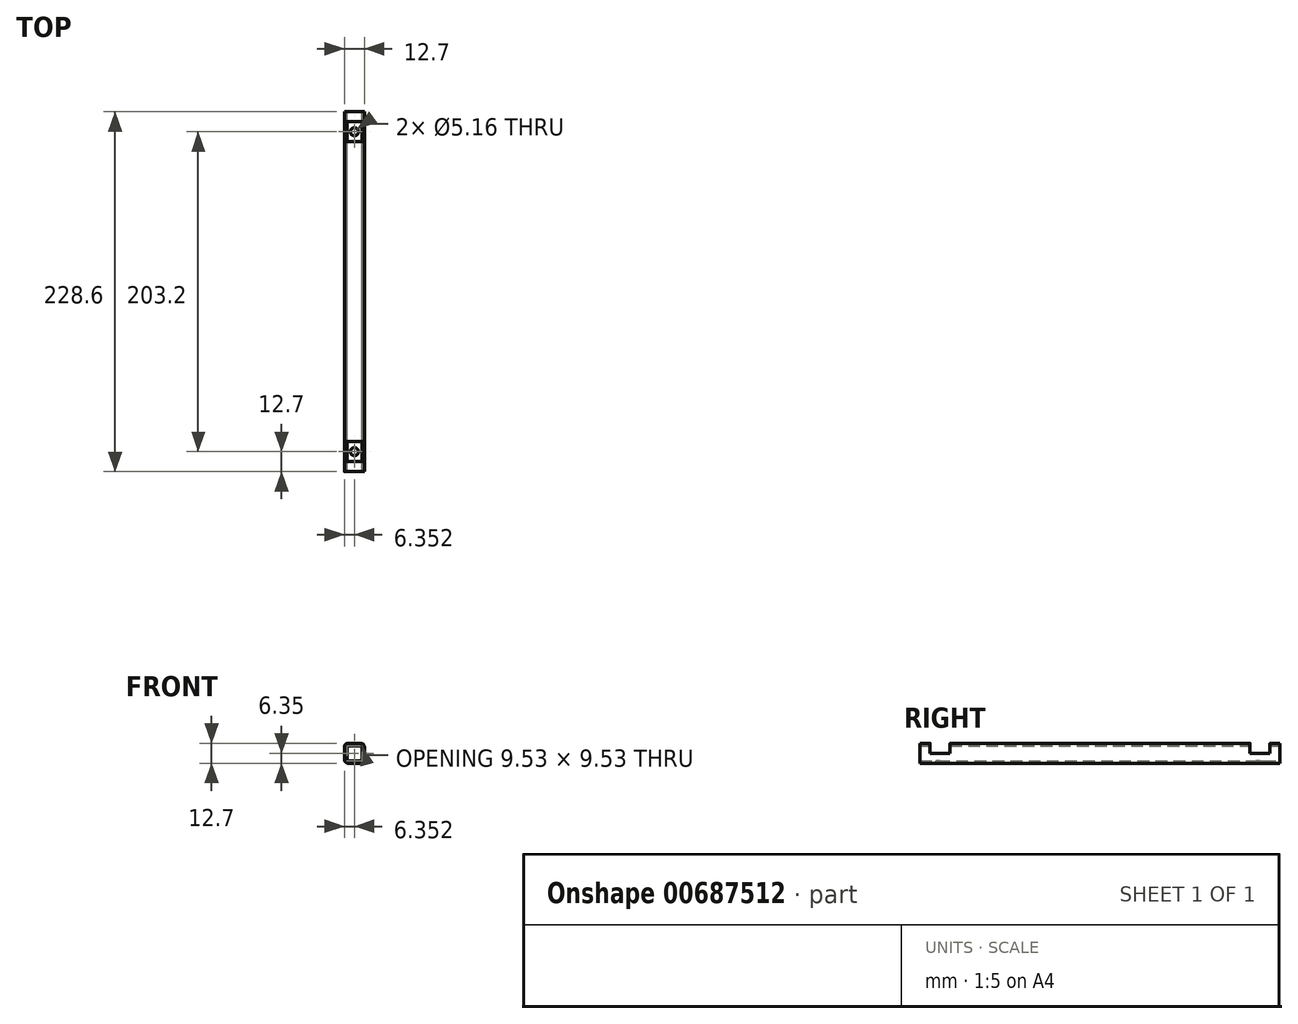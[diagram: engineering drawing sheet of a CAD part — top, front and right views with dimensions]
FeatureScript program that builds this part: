
annotation { "Feature Type Name" : "Feature", "Feature Type Description" : "" }
export const myFeature = defineFeature(function(context is Context, id is Id, definition is map)
    precondition{}
    {
        {
            var Q0;
            Q0=qCreatedBy(makeId("Front.planeOp"),FACE);
            var sketch = newSketch(context, id + "F0", { "sketchPlane" : qUnion([Q0])});
            skLineSegment(sketch, "E0.bottom", {"start": v(7.7, 0) * mm, "end": v(-0.25, 0) * mm});
            skLineSegment(sketch, "E0.top", {"start": v(7.7, -12.7) * mm, "end": v(-0.25, -12.7) * mm});
            skLineSegment(sketch, "E0.left", {"start": v(10.07, -2.38) * mm, "end": v(10.07, -10.32) * mm});
            skLineSegment(sketch, "E0.right", {"start": v(-2.63, -2.38) * mm, "end": v(-2.63, -10.32) * mm});
            skPoint(sketch, "E0.middle", {"position": v(3.72, -6.35) * mm});
            skPoint(sketch, "E1.visualSharp", {"position": v(-2.63, 0) * mm});
            skArc(sketch, "E1.filletArc", {"start": v(-0.25, 0) * mm, "mid": v(-1.93, -0.7) * mm, "end": v(-2.63, -2.38) * mm});
            skPoint(sketch, "E2.visualSharp", {"position": v(-2.63, -12.7) * mm});
            skArc(sketch, "E2.filletArc", {"start": v(-2.63, -10.32) * mm, "mid": v(-1.93, -12) * mm, "end": v(-0.25, -12.7) * mm});
            skPoint(sketch, "E3.visualSharp", {"position": v(10.07, -12.7) * mm});
            skArc(sketch, "E3.filletArc", {"start": v(7.7, -12.7) * mm, "mid": v(9.37, -12) * mm, "end": v(10.07, -10.32) * mm});
            skPoint(sketch, "E4.visualSharp", {"position": v(10.07, 0) * mm});
            skArc(sketch, "E4.filletArc", {"start": v(10.07, -2.38) * mm, "mid": v(9.37, -0.7) * mm, "end": v(7.7, 0) * mm});
            skLineSegment(sketch, "E5.bottom", {"start": v(6.9, -1.59) * mm, "end": v(0.55, -1.59) * mm});
            skLineSegment(sketch, "E5.top", {"start": v(6.9, -11.11) * mm, "end": v(0.55, -11.11) * mm});
            skLineSegment(sketch, "E5.left", {"start": v(8.48, -3.17) * mm, "end": v(8.48, -9.53) * mm});
            skLineSegment(sketch, "E5.right", {"start": v(-1.04, -3.18) * mm, "end": v(-1.04, -9.53) * mm});
            skPoint(sketch, "E6.visualSharp", {"position": v(-1.04, -1.59) * mm});
            skArc(sketch, "E6.filletArc", {"start": v(0.55, -1.59) * mm, "mid": v(-0.58, -2.05) * mm, "end": v(-1.04, -3.18) * mm});
            skPoint(sketch, "E7.visualSharp", {"position": v(8.48, -1.59) * mm});
            skArc(sketch, "E7.filletArc", {"start": v(8.48, -3.17) * mm, "mid": v(8.02, -2.05) * mm, "end": v(6.9, -1.59) * mm});
            skPoint(sketch, "E8.visualSharp", {"position": v(8.48, -11.11) * mm});
            skArc(sketch, "E8.filletArc", {"start": v(6.9, -11.11) * mm, "mid": v(8.02, -10.65) * mm, "end": v(8.48, -9.53) * mm});
            skPoint(sketch, "E9.visualSharp", {"position": v(-1.04, -11.11) * mm});
            skArc(sketch, "E9.filletArc", {"start": v(-1.04, -9.53) * mm, "mid": v(-0.58, -10.65) * mm, "end": v(0.55, -11.11) * mm});
            skSolve(sketch);
        }
        {
            var Q0;
            Q0=qSketchRegion(id+"F0",true);
            extrude(context, id + "F1", {"entities" : qUnion([Q0]), "depth" : 228.6 * mm, "offsetDistance" : 25.4 * mm});
        }
        {
            var Q0;
            Q0=qCreatedBy(makeId("Right.planeOp"),FACE);
            var sketch = newSketch(context, id + "F2", { "sketchPlane" : qUnion([Q0])});
            skLineSegment(sketch, "E10.bottom", {"start": v(-222.25, 0) * mm, "end": v(-209.55, 0) * mm});
            skLineSegment(sketch, "E10.top", {"start": v(-222.25, -6.35) * mm, "end": v(-209.55, -6.35) * mm});
            skLineSegment(sketch, "E10.left", {"start": v(-222.25, 0) * mm, "end": v(-222.25, -6.35) * mm});
            skLineSegment(sketch, "E10.right", {"start": v(-209.55, 0) * mm, "end": v(-209.55, -6.35) * mm});
            skLineSegment(sketch, "E11.bottom", {"start": v(-6.35, 0) * mm, "end": v(-19.05, 0) * mm});
            skLineSegment(sketch, "E11.top", {"start": v(-6.35, -6.35) * mm, "end": v(-19.05, -6.35) * mm});
            skLineSegment(sketch, "E11.left", {"start": v(-6.35, 0) * mm, "end": v(-6.35, -6.35) * mm});
            skLineSegment(sketch, "E11.right", {"start": v(-19.05, 0) * mm, "end": v(-19.05, -6.35) * mm});
            skSolve(sketch);
        }
        {
            var Q0;
            Q0=qSketchRegion(id+"F2",true);
            extrude(context, id + "F3", {"entities" : qUnion([Q0]), "operationType" : NewBodyOperationType.REMOVE, "depth" : 11.94 * mm, "offsetDistance" : 25.4 * mm, "hasSecondDirection" : true, "secondDirectionOppositeDirection" : true, "secondDirectionDepth" : 25.4 * mm});
        }
        {
            var Q0;
            Q0=qCreatedBy(makeId("Top.planeOp"),FACE);
            var sketch = newSketch(context, id + "F4", { "sketchPlane" : qUnion([Q0])});
            skCircle(sketch, "E12", {"center": v(3.72, -12.7) * mm, "radius": 2.58 * mm});
            skCircle(sketch, "E13", {"center": v(3.72, -215.9) * mm, "radius": 2.58 * mm});
            skSolve(sketch);
        }
        {
            var Q0;
            Q0=qSketchRegion(id+"F4",true);
            extrude(context, id + "F5", {"entities" : qUnion([Q0]), "operationType" : NewBodyOperationType.REMOVE, "oppositeDirection" : true, "depth" : 12.7 * mm, "offsetDistance" : 25.4 * mm});
        }
    });
